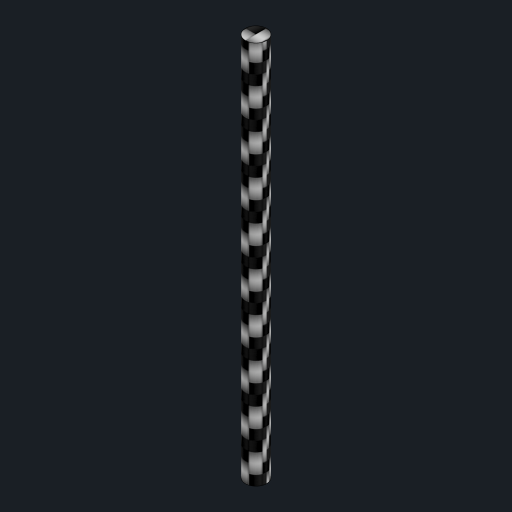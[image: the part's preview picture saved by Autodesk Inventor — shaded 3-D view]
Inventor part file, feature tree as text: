
AUTODESK INVENTOR PART (.ipt)
format: ipt  version: 2023 (Build 270158000, 158)  size: 102,912 bytes
history: native  units: mm
features: other x1, extrude x1, sketch x1
ambient origin geometry x8: Origin, YZ Plane, XZ Plane, XY Plane, X Axis, Y Axis, Z Axis, Center Point
bodies: Body1 (feature_tree)
feature tree (3):
  other  "ソリッド1"
  extrude  "押し出し1"  Depth=2.0mm
  sketch  "スケッチ1"
